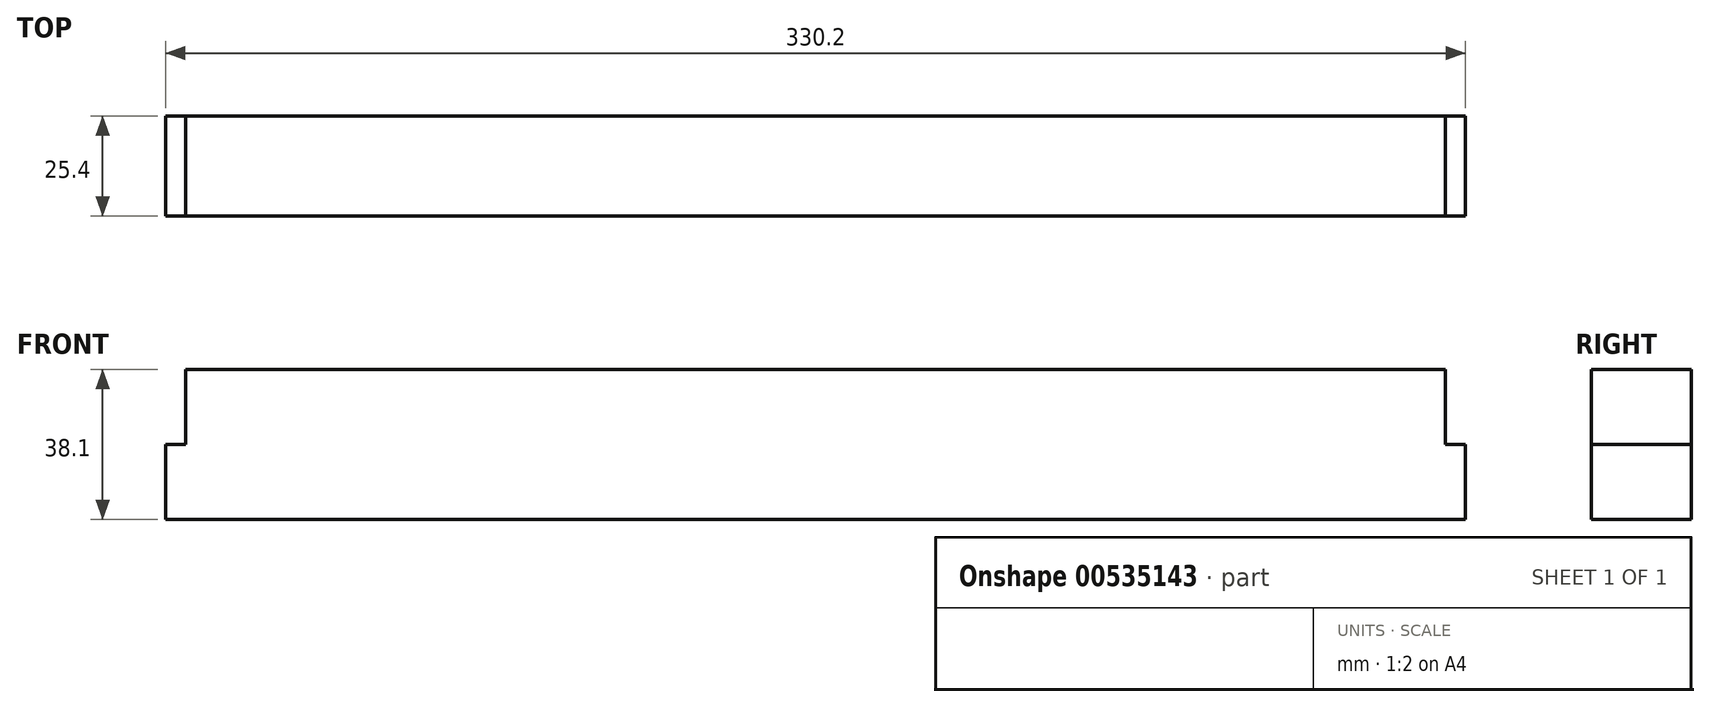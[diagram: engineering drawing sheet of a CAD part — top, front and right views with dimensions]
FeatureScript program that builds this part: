
annotation { "Feature Type Name" : "Feature", "Feature Type Description" : "" }
export const myFeature = defineFeature(function(context is Context, id is Id, definition is map)
    precondition{}
    {
        {
            var Q0;
            Q0=qCreatedBy(makeId("Front.planeOp"),FACE);
            var sketch = newSketch(context, id + "F0", { "sketchPlane" : qUnion([Q0])});
            skLineSegment(sketch, "E0.bottom", {"start": v(0, 0) * mm, "end": v(330.2, 0) * mm});
            skLineSegment(sketch, "E0.top", {"start": v(5.08, 38.1) * mm, "end": v(325.12, 38.1) * mm});
            skLineSegment(sketch, "E0.left", {"start": v(0, 0) * mm, "end": v(0, 19.05) * mm});
            skLineSegment(sketch, "E0.right", {"start": v(330.2, 0) * mm, "end": v(330.2, 19.05) * mm});
            skLineSegment(sketch, "E1.top", {"start": v(0, 19.05) * mm, "end": v(5.08, 19.05) * mm});
            skLineSegment(sketch, "E1.right", {"start": v(5.08, 38.1) * mm, "end": v(5.08, 19.05) * mm});
            skLineSegment(sketch, "E2.top", {"start": v(330.2, 19.05) * mm, "end": v(325.12, 19.05) * mm});
            skLineSegment(sketch, "E2.right", {"start": v(325.12, 38.1) * mm, "end": v(325.12, 19.05) * mm});
            skSolve(sketch);
        }
        {
            var Q0;
            Q0=qSketchRegion(id+"F0",true);
            extrude(context, id + "F1", {"entities" : qUnion([Q0]), "depth" : 25.4 * mm});
        }
    });
